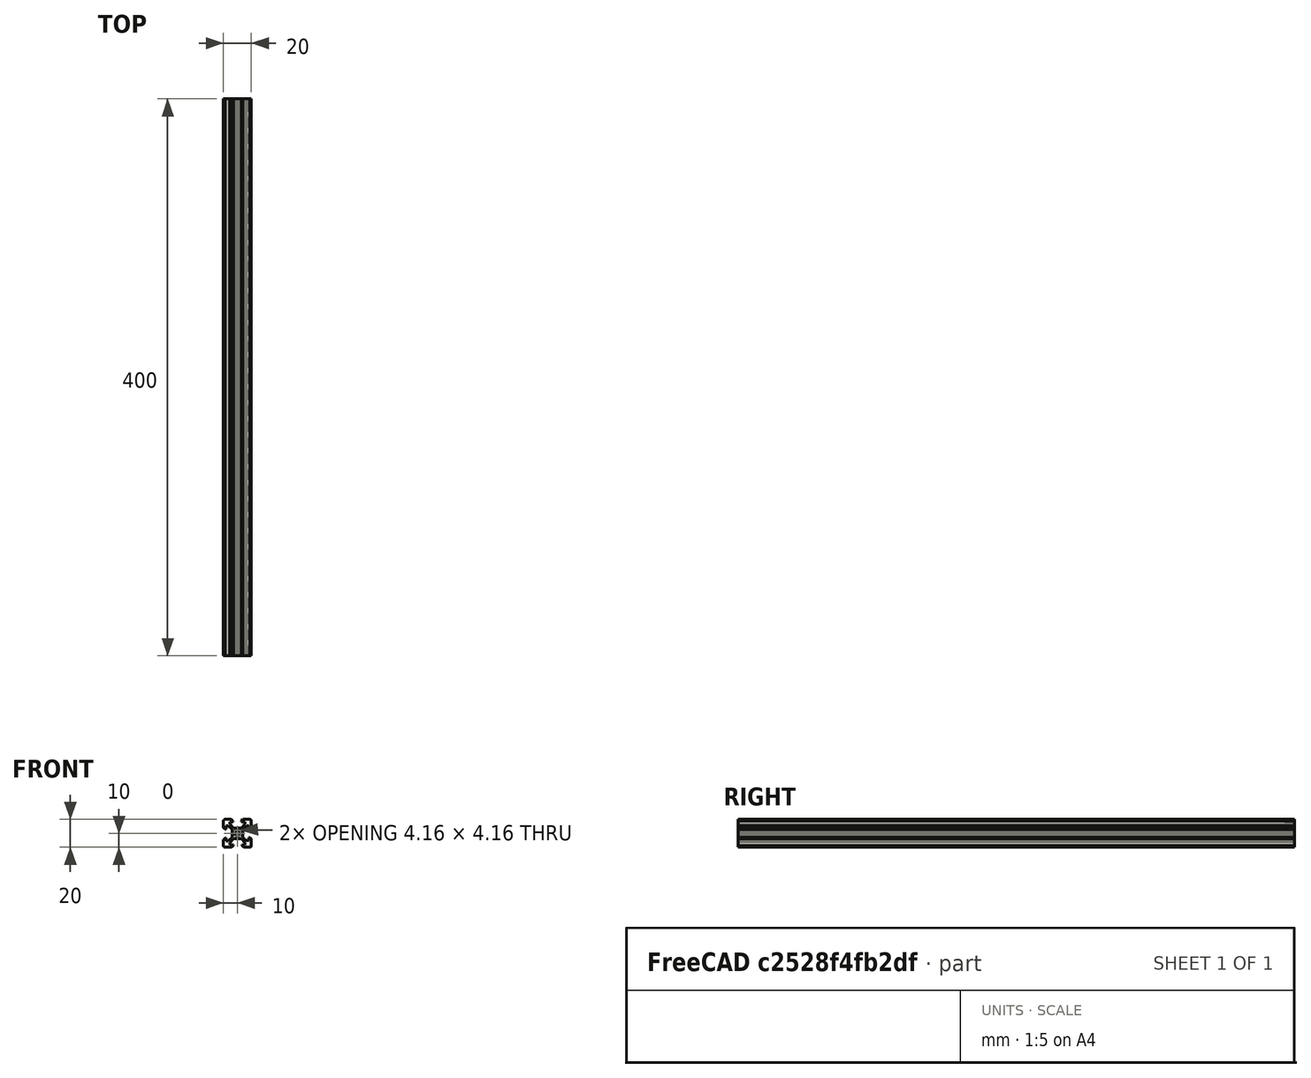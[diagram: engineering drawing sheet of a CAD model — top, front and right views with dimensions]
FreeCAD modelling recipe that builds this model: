
FCSTD DOCUMENT  (FreeCAD 0.20R29410 (Git))
Label: 40cm_2020_aluminum_extrusion
License: All rights reserved
LicenseURL: http://en.wikipedia.org/wiki/All_rights_reserved
objects: Part::Refine×2, App::MeasureDistance×2, Part::Feature×1, PartDesign::FeatureBase×1, PartDesign::Pad×1, PartDesign::Body×1
note: 7 computed .brp shape members not serialized (recipe doc carries the construction recipe); baked Part::Feature solids carry a one-line shape summary decoded from their .brp

FEATURE [Part::Feature] _020_aluminum_extrusion_face001002_solid  label="_020_aluminum_extrusion_face001002 (Solid)"
  shape: bbox 20 x 7 x 20 mm, 1316 faces (baked)
FEATURE [Part::Refine] _020_aluminum_extrusion_face001002_solid001  label="_020_aluminum_extrusion_face001002 (Solid)001"
  Source = -> _020_aluminum_extrusion_face001002_solid
FEATURE [App::MeasureDistance] Distance  label="Distance: 7.01 mm"
  Distance = 7.00618
  P1 = (-330,0,146.819)
  P2 = (-330,6.99856,146.492)
FEATURE [PartDesign::FeatureBase] BaseFeature
  BaseFeature = -> _020_aluminum_extrusion_face001002_solid001
FEATURE [PartDesign::Pad] Pad
  BaseFeature = -> BaseFeature
  Direction = (0,-1,0)
  Length = 393
  Length2 = 10
  Profile = -> BaseFeature [Face2]
  Type = 0
FEATURE [PartDesign::Body] Body
  BaseFeature = -> _020_aluminum_extrusion_face001002_solid001
  Group = -> [BaseFeature,Pad]
  Origin = -> Origin
  Tip = -> Pad
FEATURE [App::MeasureDistance] Distance001  label="Distance: 399.99 mm"
  Distance = 399.992
  P1 = (-330.024,-393,144.543)
  P2 = (-330.027,6.99189,144.425)
FEATURE [Part::Refine] Pad001  label="40cm_2020_aluminum_extrusion"
  Source = -> Pad
